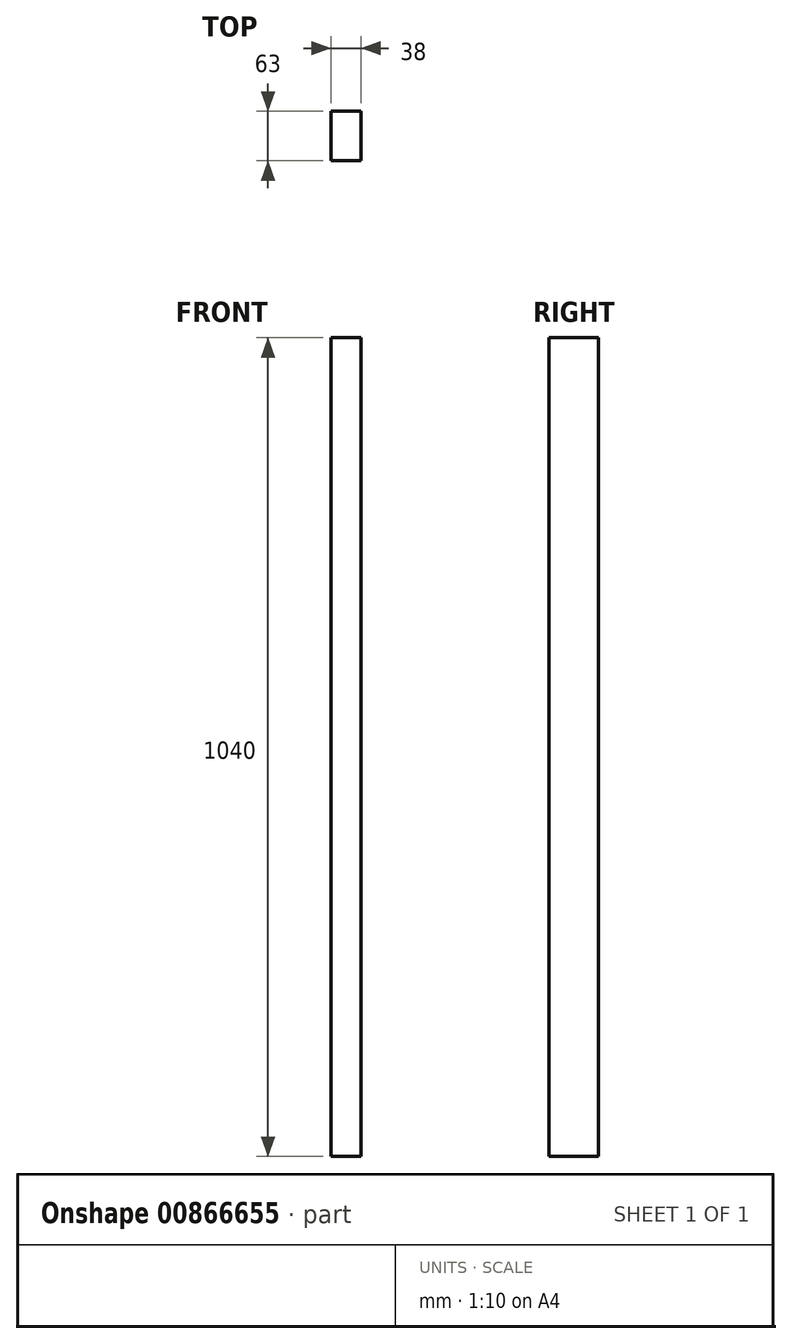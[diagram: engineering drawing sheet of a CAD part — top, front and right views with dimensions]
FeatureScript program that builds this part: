
annotation { "Feature Type Name" : "Feature", "Feature Type Description" : "" }
export const myFeature = defineFeature(function(context is Context, id is Id, definition is map)
    precondition{}
    {
        {
            var Q0;
            Q0=qCreatedBy(makeId("Top.planeOp"),FACE);
            var sketch = newSketch(context, id + "F0", { "sketchPlane" : qUnion([Q0])});
            skLineSegment(sketch, "E0.bottom", {"start": v(-19, 31.5) * mm, "end": v(19, 31.5) * mm});
            skLineSegment(sketch, "E0.top", {"start": v(-19, -31.5) * mm, "end": v(19, -31.5) * mm});
            skLineSegment(sketch, "E0.left", {"start": v(-19, 31.5) * mm, "end": v(-19, -31.5) * mm});
            skLineSegment(sketch, "E0.right", {"start": v(19, 31.5) * mm, "end": v(19, -31.5) * mm});
            skPoint(sketch, "E0.middle", {"position": v(0, 0) * mm});
            skSolve(sketch);
        }
        {
            var Q0;
            Q0 = qSketchRegion(id + "F0", true);
            extrude(context, id + "F1", {"entities" : qUnion([Q0]), "depth" : 1040 * mm, "offsetDistance" : 25 * mm});
        }
    });
